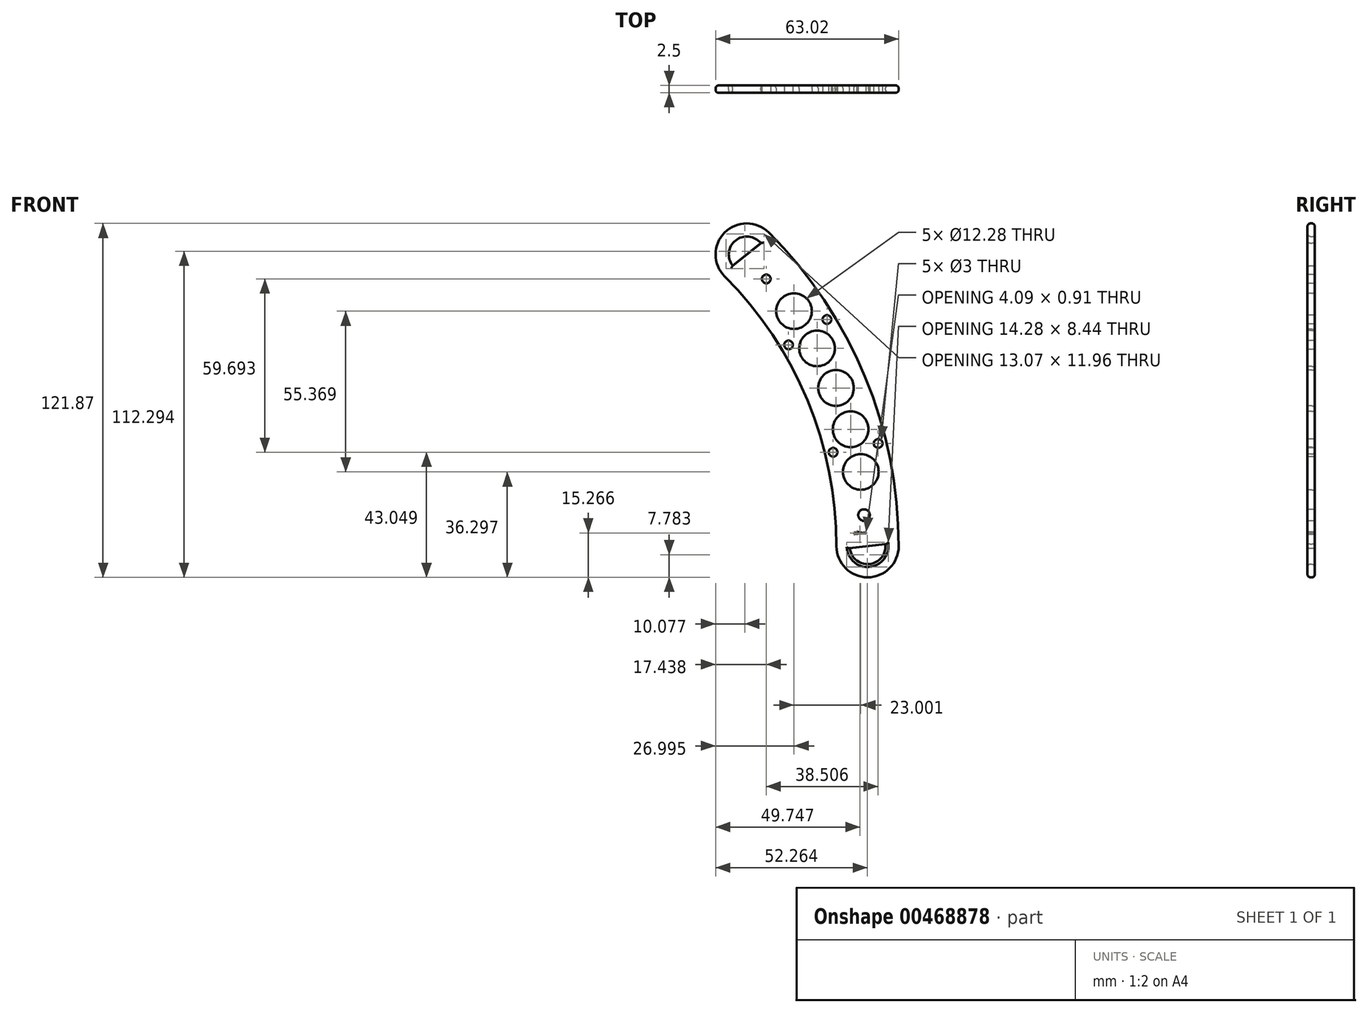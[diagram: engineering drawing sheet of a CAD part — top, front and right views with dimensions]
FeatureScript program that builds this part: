
annotation { "Feature Type Name" : "Feature", "Feature Type Description" : "" }
export const myFeature = defineFeature(function(context is Context, id is Id, definition is map)
    precondition{}
    {
        {
            var Q0;
            Q0=qCreatedBy(makeId("Front.planeOp"),FACE);
            var sketch = newSketch(context, id + "F0", { "sketchPlane" : qUnion([Q0])});
            skCircle(sketch, "E0", {"center": v(0, 0) * mm, "radius": 152.8 * mm});
            skCircle(sketch, "E1", {"center": v(0, 0) * mm, "radius": 131.4 * mm});
            skLineSegment(sketch, "E2", {"start": v(0, 0) * mm, "end": v(152.8, 0) * mm, "construction": true});
            skLineSegment(sketch, "E3", {"start": v(0, 0) * mm, "end": v(108.04, 108.04) * mm, "construction": true});
            skPoint(sketch, "E4", {"position": v(92.9, 92.9) * mm});
            skPoint(sketch, "E5", {"position": v(108.04, 108.04) * mm});
            skPoint(sketch, "E6", {"position": v(131.4, 0) * mm});
            skPoint(sketch, "E7", {"position": v(152.8, 0) * mm});
            skCircle(sketch, "E8", {"center": v(100.47, 100.47) * mm, "radius": 10.7 * mm});
            skCircle(sketch, "E9", {"center": v(142.1, 0) * mm, "radius": 10.7 * mm});
            skLineSegment(sketch, "E10", {"start": v(142.1, 0) * mm, "end": v(148.23, 0.7) * mm});
            skLineSegment(sketch, "E11", {"start": v(142.1, 0) * mm, "end": v(135.94, -0.7) * mm});
            skLineSegment(sketch, "E12", {"start": v(148.23, 0.7) * mm, "end": v(144.58, 32.71) * mm});
            skLineSegment(sketch, "E13", {"start": v(135.94, -0.7) * mm, "end": v(132.3, 31.31) * mm});
            skLineSegment(sketch, "E14", {"start": v(132.3, 31.31) * mm, "end": v(144.58, 32.71) * mm});
            skLineSegment(sketch, "E15", {"start": v(100.47, 100.47) * mm, "end": v(105.3, 104.33) * mm});
            skLineSegment(sketch, "E16", {"start": v(100.47, 100.47) * mm, "end": v(95.64, 96.62) * mm});
            skLineSegment(sketch, "E17", {"start": v(120.53, 75.25) * mm, "end": v(125.41, 79.16) * mm});
            skLineSegment(sketch, "E18", {"start": v(120.53, 75.25) * mm, "end": v(115.75, 71.44) * mm});
            skLineSegment(sketch, "E19", {"start": v(105.3, 104.33) * mm, "end": v(125.41, 79.16) * mm});
            skLineSegment(sketch, "E20", {"start": v(95.64, 96.62) * mm, "end": v(115.75, 71.44) * mm});
            skLineSegment(sketch, "E21", {"start": v(135.42, 3.88) * mm, "end": v(147.7, 5.28) * mm});
            skLineSegment(sketch, "E22", {"start": v(132.82, 26.73) * mm, "end": v(145.1, 28.13) * mm});
            skLineSegment(sketch, "E23", {"start": v(112.88, 75.04) * mm, "end": v(122.53, 82.76) * mm});
            skLineSegment(sketch, "E24", {"start": v(98.52, 93.01) * mm, "end": v(108.18, 100.73) * mm});
            skCircle(sketch, "E25", {"center": v(0, 0) * mm, "radius": 148.23 * mm, "construction": true});
            skCircle(sketch, "E26", {"center": v(0, 0) * mm, "radius": 135.95 * mm, "construction": true});
            skCircle(sketch, "E27", {"center": v(141.82, 2.29) * mm, "radius": 1 * mm});
            skCircle(sketch, "E28", {"center": v(138.7, 29.72) * mm, "radius": 1 * mm});
            skCircle(sketch, "E29", {"center": v(140.86, 10.72) * mm, "radius": 6.18 * mm});
            skLineSegment(sketch, "E30", {"start": v(122.53, 82.76) * mm, "end": v(115.75, 71.44) * mm, "construction": true});
            skLineSegment(sketch, "E31", {"start": v(112.88, 75.04) * mm, "end": v(125.41, 79.16) * mm, "construction": true});
            skCircle(sketch, "E32", {"center": v(101.91, 98.67) * mm, "radius": 1 * mm});
            skCircle(sketch, "E33", {"center": v(119.14, 77.1) * mm, "radius": 1 * mm});
            skCircle(sketch, "E34", {"center": v(107.2, 92.04) * mm, "radius": 6.18 * mm});
            skLineSegment(sketch, "E35", {"start": v(132.82, 26.73) * mm, "end": v(144.58, 32.71) * mm, "construction": true});
            skLineSegment(sketch, "E36", {"start": v(145.1, 28.13) * mm, "end": v(132.3, 31.31) * mm, "construction": true});
            skCircle(sketch, "E37", {"center": v(100.47, 100.47) * mm, "radius": 6.18 * mm});
            skCircle(sketch, "E38", {"center": v(142.1, 0) * mm, "radius": 6.19 * mm});
            skLineSegment(sketch, "E39", {"start": v(135.42, 3.88) * mm, "end": v(148.23, 0.7) * mm, "construction": true});
            skLineSegment(sketch, "E40", {"start": v(147.7, 5.28) * mm, "end": v(135.94, -0.7) * mm, "construction": true});
            skLineSegment(sketch, "E41", {"start": v(148.23, 0.7) * mm, "end": v(148.24, 0.7) * mm});
            skSolve(sketch);
        }
        {
            var Q0;
            {var subQ16=sQuery(id+"F0.wireOp",EDGE,"E18");Q0=makeQuery(id+"F0.imprint","IMPRINT",FACE,{"disambiguationData":[TD([[makeQuery(id+"F0.imprint","IMPRINT",EDGE,{"derivedFrom":subQ16}),1.0]])]});}
            var Q1;
            {var subQ14=sQuery(id+"F0.wireOp",EDGE,"E17");Q1=makeQuery(id+"F0.imprint","IMPRINT",FACE,{"disambiguationData":[TD([[makeQuery(id+"F0.imprint","IMPRINT",EDGE,{"derivedFrom":subQ14}),-1.0]])]});}
            var Q2;
            {var subQ3=sQuery(id+"F0.wireOp",EDGE,"oQQra7B9-EMDj-B2YQ-GpEd-beqhVWcHA2Qh");var subQ5=sQuery(id+"F0.wireOp",EDGE,"E22");var subQ9=makeQuery(id+"F0.imprint","INTERSECT",VERTEX,{"derivedFrom":[subQ3,subQ5]});Q2=makeQuery(id+"F0.imprint","IMPRINT",FACE,{"disambiguationData":[TD([[makeQuery(id+"F0.imprint","IMPRINT",EDGE,{"disambiguationData":[TD([[subQ9,-1.0]])],"derivedFrom":subQ3}),-1.0]])]});}
            var Q3;
            {var subQ3=sQuery(id+"F0.wireOp",EDGE,"oQQra7B9-EMDj-B2YQ-GpEd-beqhVWcHA2Qh");var subQ5=sQuery(id+"F0.wireOp",EDGE,"E22");var subQ9=makeQuery(id+"F0.imprint","INTERSECT",VERTEX,{"derivedFrom":[subQ3,subQ5]});Q3=makeQuery(id+"F0.imprint","IMPRINT",FACE,{"disambiguationData":[TD([[makeQuery(id+"F0.imprint","IMPRINT",EDGE,{"disambiguationData":[TD([[subQ9,-1.0]])],"derivedFrom":subQ3}),1.0]])]});}
            var Q4;
            {var subQ5=sQuery(id+"F0.wireOp",EDGE,"E9");var subQ8=makeQuery(id+"F0.imprint","INTERSECT",VERTEX,{"derivedFrom":[sQuery(id+"F0.wireOp",EDGE,"E1"),subQ5]});Q4=makeQuery(id+"F0.imprint","IMPRINT",FACE,{"disambiguationData":[TD([[makeQuery(id+"F0.imprint","IMPRINT",EDGE,{"disambiguationData":[TD([[subQ8,1.0]])],"derivedFrom":subQ5}),1.0]])]});}
            var Q5;
            {var subQ1=sQuery(id+"F0.wireOp",EDGE,"E9");var subQ5=makeQuery(id+"F0.imprint","INTERSECT",VERTEX,{"derivedFrom":[sQuery(id+"F0.wireOp",EDGE,"E0"),subQ1]});Q5=makeQuery(id+"F0.imprint","IMPRINT",FACE,{"disambiguationData":[TD([[makeQuery(id+"F0.imprint","IMPRINT",EDGE,{"disambiguationData":[TD([[subQ5,-1.0]])],"derivedFrom":subQ1}),1.0]])]});}
            var Q6;
            {var subQ1=sQuery(id+"F0.wireOp",EDGE,"E13");var subQ3=sQuery(id+"F0.wireOp",EDGE,"E21");var subQ4=makeQuery(id+"F0.imprint","INTERSECT",VERTEX,{"derivedFrom":[subQ1,subQ3]});Q6=makeQuery(id+"F0.imprint","IMPRINT",FACE,{"disambiguationData":[TD([[makeQuery(id+"F0.imprint","IMPRINT",EDGE,{"disambiguationData":[TD([[subQ4,-1.0]])],"derivedFrom":subQ3}),-1.0]])]});}
            var Q7;
            {var subQ1=sQuery(id+"F0.wireOp",EDGE,"E12");var subQ3=sQuery(id+"F0.wireOp",EDGE,"E21");var subQ4=makeQuery(id+"F0.imprint","INTERSECT",VERTEX,{"derivedFrom":[subQ1,subQ3]});Q7=makeQuery(id+"F0.imprint","IMPRINT",FACE,{"disambiguationData":[TD([[makeQuery(id+"F0.imprint","IMPRINT",EDGE,{"disambiguationData":[TD([[subQ4,1.0]])],"derivedFrom":subQ3}),-1.0]])]});}
            var Q8;
            {var subQ4=sQuery(id+"F0.wireOp",EDGE,"E8");var subQ5=makeQuery(id+"F0.imprint","INTERSECT",VERTEX,{"derivedFrom":[sQuery(id+"F0.wireOp",EDGE,"E0"),subQ4]});Q8=makeQuery(id+"F0.imprint","IMPRINT",FACE,{"disambiguationData":[TD([[makeQuery(id+"F0.imprint","IMPRINT",EDGE,{"disambiguationData":[TD([[subQ5,-1.0]])],"derivedFrom":subQ4}),1.0]])]});}
            var Q9;
            {var subQ5=sQuery(id+"F0.wireOp",EDGE,"E8");var subQ9=makeQuery(id+"F0.imprint","INTERSECT",VERTEX,{"derivedFrom":[sQuery(id+"F0.wireOp",EDGE,"E1"),subQ5]});Q9=makeQuery(id+"F0.imprint","IMPRINT",FACE,{"disambiguationData":[TD([[makeQuery(id+"F0.imprint","IMPRINT",EDGE,{"disambiguationData":[TD([[subQ9,1.0]])],"derivedFrom":subQ5}),1.0]])]});}
            var Q10;
            {var subQ1=sQuery(id+"F0.wireOp",EDGE,"E20");var subQ3=sQuery(id+"F0.wireOp",EDGE,"E24");var subQ4=makeQuery(id+"F0.imprint","INTERSECT",VERTEX,{"derivedFrom":[subQ1,subQ3]});Q10=makeQuery(id+"F0.imprint","IMPRINT",FACE,{"disambiguationData":[TD([[makeQuery(id+"F0.imprint","IMPRINT",EDGE,{"disambiguationData":[TD([[subQ4,-1.0]])],"derivedFrom":subQ3}),1.0]])]});}
            var Q11;
            {var subQ4=sQuery(id+"F0.wireOp",EDGE,"E16");Q11=makeQuery(id+"F0.imprint","IMPRINT",FACE,{"disambiguationData":[TD([[makeQuery(id+"F0.imprint","IMPRINT",EDGE,{"derivedFrom":subQ4}),1.0]])]});}
            var Q12;
            {var subQ0=sQuery(id+"F0.wireOp",EDGE,"E15");Q12=makeQuery(id+"F0.imprint","IMPRINT",FACE,{"disambiguationData":[TD([[makeQuery(id+"F0.imprint","IMPRINT",EDGE,{"derivedFrom":subQ0}),-1.0]])]});}
            var Q13;
            {var subQ1=sQuery(id+"F0.wireOp",EDGE,"E19");var subQ3=sQuery(id+"F0.wireOp",EDGE,"E24");var subQ4=makeQuery(id+"F0.imprint","INTERSECT",VERTEX,{"derivedFrom":[subQ1,subQ3]});Q13=makeQuery(id+"F0.imprint","IMPRINT",FACE,{"disambiguationData":[TD([[makeQuery(id+"F0.imprint","IMPRINT",EDGE,{"disambiguationData":[TD([[subQ4,1.0]])],"derivedFrom":subQ3}),1.0]])]});}
            var Q14;
            {var subQ1=sQuery(id+"F0.wireOp",EDGE,"E18");Q14=makeQuery(id+"F0.imprint","IMPRINT",FACE,{"disambiguationData":[TD([[makeQuery(id+"F0.imprint","IMPRINT",EDGE,{"derivedFrom":subQ1}),-1.0]])]});}
            var Q15;
            {var subQ1=sQuery(id+"F0.wireOp",EDGE,"E17");Q15=makeQuery(id+"F0.imprint","IMPRINT",FACE,{"disambiguationData":[TD([[makeQuery(id+"F0.imprint","IMPRINT",EDGE,{"derivedFrom":subQ1}),1.0]])]});}
            var Q16;
            {var subQ0=sQuery(id+"F0.wireOp",EDGE,"E14");Q16=makeQuery(id+"F0.imprint","IMPRINT",FACE,{"disambiguationData":[TD([[makeQuery(id+"F0.imprint","IMPRINT",EDGE,{"derivedFrom":subQ0}),-1.0]])]});}
            var Q17;
            {var subQ5=sQuery(id+"F0.wireOp",EDGE,"E10");Q17=makeQuery(id+"F0.imprint","IMPRINT",FACE,{"disambiguationData":[TD([[makeQuery(id+"F0.imprint","IMPRINT",EDGE,{"derivedFrom":subQ5}),1.0]])]});}
            var Q18;
            Q18=makeQuery(id+"F0.imprint","IMPRINT",FACE,{"disambiguationData":[TD([[makeQuery(id+"F0.imprint","IMPRINT",EDGE,{"derivedFrom":sQuery(id+"F0.wireOp",EDGE,"E27")}),-1.0]])]});
            var Q19;
            {var subQ0=sQuery(id+"F0.wireOp",EDGE,"E41");Q19=makeQuery(id+"F0.imprint","IMPRINT",FACE,{"disambiguationData":[TD([[makeQuery(id+"F0.imprint","IMPRINT",EDGE,{"derivedFrom":subQ0}),1.0]])]});}
            extrude(context, id + "F1", {"entities" : qUnion([Q0, Q1, Q2, Q3, Q4, Q5, Q6, Q7, Q8, Q9, Q10, Q11, Q12, Q13, Q14, Q15, Q16, Q17, Q18, Q19]), "depth" : 2.5 * mm});
        }
        {
            var Q0;
            Q0=makeQuery(id+"F1.opExtrude","CAP_FACE",FACE,{"disambiguationData":[OSD([sQuery(id+"F0.wireOp",EDGE,"E0"),sQuery(id+"F0.wireOp",EDGE,"E1"),sQuery(id+"F0.wireOp",EDGE,"E8"),sQuery(id+"F0.wireOp",EDGE,"E9"),sQuery(id+"F0.wireOp",EDGE,"E10"),sQuery(id+"F0.wireOp",EDGE,"E11"),sQuery(id+"F0.wireOp",EDGE,"E12"),sQuery(id+"F0.wireOp",EDGE,"E13"),sQuery(id+"F0.wireOp",EDGE,"E15"),sQuery(id+"F0.wireOp",EDGE,"E16"),sQuery(id+"F0.wireOp",EDGE,"E19"),sQuery(id+"F0.wireOp",EDGE,"E20"),sQuery(id+"F0.wireOp",EDGE,"E21"),sQuery(id+"F0.wireOp",EDGE,"E22"),sQuery(id+"F0.wireOp",EDGE,"E23"),sQuery(id+"F0.wireOp",EDGE,"E24"),sQuery(id+"F0.wireOp",EDGE,"E27"),sQuery(id+"F0.wireOp",EDGE,"E28"),sQuery(id+"F0.wireOp",EDGE,"E32"),sQuery(id+"F0.wireOp",EDGE,"E33"),sQuery(id+"F0.wireOp",EDGE,"E37"),sQuery(id+"F0.wireOp",EDGE,"E38")])],"isStart":false});
            var sketch = newSketch(context, id + "F2", { "sketchPlane" : qUnion([Q0])});
            skCircle(sketch, "E42", {"center": v(136.26, 40.28) * mm, "radius": 6.14 * mm});
            skCircle(sketch, "E43", {"center": v(124.7, 68.12) * mm, "radius": 6.14 * mm});
            skCircle(sketch, "E44", {"center": v(131.22, 54.5) * mm, "radius": 6.14 * mm});
            skCircle(sketch, "E45", {"center": v(0, 0) * mm, "radius": 142.1 * mm, "construction": true});
            skLineSegment(sketch, "E46", {"start": v(0, 0) * mm, "end": v(136.26, 40.28) * mm, "construction": true});
            skLineSegment(sketch, "E47", {"start": v(0, 0) * mm, "end": v(131.22, 54.5) * mm, "construction": true});
            skLineSegment(sketch, "E48", {"start": v(0, 0) * mm, "end": v(124.7, 68.12) * mm, "construction": true});
            skCircle(sketch, "E49", {"center": v(0, 0) * mm, "radius": 152.8 * mm, "construction": true});
            skCircle(sketch, "E50", {"center": v(0, 0) * mm, "radius": 131.4 * mm, "construction": true});
            skCircle(sketch, "E51", {"center": v(0, 0) * mm, "radius": 135.95 * mm, "construction": true});
            skCircle(sketch, "E52", {"center": v(0, 0) * mm, "radius": 148.23 * mm, "construction": true});
            skLineSegment(sketch, "E53", {"start": v(112.88, 75.04) * mm, "end": v(119.3, 65.18) * mm, "construction": true});
            skLineSegment(sketch, "E54", {"start": v(119.3, 65.18) * mm, "end": v(118, 79.14) * mm, "construction": true});
            skLineSegment(sketch, "E55", {"start": v(118, 79.14) * mm, "end": v(130.08, 71.07) * mm, "construction": true});
            skLineSegment(sketch, "E56", {"start": v(130.08, 71.07) * mm, "end": v(122.53, 82.76) * mm, "construction": true});
            skLineSegment(sketch, "E57", {"start": v(122.53, 82.76) * mm, "end": v(118, 79.14) * mm});
            skLineSegment(sketch, "E58", {"start": v(112.88, 75.04) * mm, "end": v(118, 79.14) * mm});
            skLineSegment(sketch, "E59", {"start": v(126.3, 76.91) * mm, "end": v(130.43, 79.57) * mm, "construction": true});
            skCircle(sketch, "E60", {"center": v(128.1, 78.07) * mm, "radius": 1 * mm});
            skLineSegment(sketch, "E61", {"start": v(130.37, 38.54) * mm, "end": v(132.82, 26.73) * mm});
            skLineSegment(sketch, "E62", {"start": v(145.1, 28.13) * mm, "end": v(142.22, 41.78) * mm});
            skLineSegment(sketch, "E63", {"start": v(131.6, 32.64) * mm, "end": v(127.49, 31.79) * mm});
            skLineSegment(sketch, "E64", {"start": v(143.66, 34.96) * mm, "end": v(148.5, 35.98) * mm});
            skCircle(sketch, "E65", {"center": v(130.21, 32.35) * mm, "radius": 1 * mm});
            skCircle(sketch, "E66", {"center": v(145.71, 35.4) * mm, "radius": 1 * mm});
            skLineSegment(sketch, "E67", {"start": v(116.1, 70.11) * mm, "end": v(112.55, 67.8) * mm, "construction": true});
            skCircle(sketch, "E68", {"center": v(114.87, 69.32) * mm, "radius": 1 * mm});
            skLineSegment(sketch, "E69", {"start": v(0, 0) * mm, "end": v(116.76, 80.97) * mm, "construction": true});
            skLineSegment(sketch, "E70", {"start": v(0, 0) * mm, "end": v(139.77, 25.6) * mm, "construction": true});
            skCircle(sketch, "E71", {"center": v(139.77, 25.6) * mm, "radius": 6.14 * mm});
            skCircle(sketch, "E72", {"center": v(116.76, 80.97) * mm, "radius": 6.14 * mm});
            skSolve(sketch);
        }
        {
            var Q0;
            Q0=makeQuery(id+"F2.imprint","IMPRINT",FACE,{"disambiguationData":[TD([[makeQuery(id+"F2.imprint","IMPRINT",EDGE,{"derivedFrom":sQuery(id+"F2.wireOp",EDGE,"E43")}),1.0]])]});
            var Q1;
            Q1=makeQuery(id+"F2.imprint","IMPRINT",FACE,{"disambiguationData":[TD([[makeQuery(id+"F2.imprint","IMPRINT",EDGE,{"derivedFrom":sQuery(id+"F2.wireOp",EDGE,"E44")}),1.0]])]});
            var Q2;
            Q2=makeQuery(id+"F2.imprint","IMPRINT",FACE,{"disambiguationData":[TD([[makeQuery(id+"F2.imprint","IMPRINT",EDGE,{"derivedFrom":sQuery(id+"F2.wireOp",EDGE,"E42")}),1.0]])]});
            var Q3;
            {var subQ0=sQuery(id+"F2.wireOp",EDGE,"E56");var subQ1=sQuery(id+"F2.wireOp",EDGE,"E43");var subQ2=makeQuery(id+"F2.imprint","INTERSECT",VERTEX,{"derivedFrom":[subQ1,subQ0]});Q3=makeQuery(id+"F2.imprint","IMPRINT",FACE,{"disambiguationData":[TD([[makeQuery(id+"F2.imprint","IMPRINT",EDGE,{"disambiguationData":[TD([[subQ2,-1.0]])],"derivedFrom":subQ1}),1.0]])]});}
            var Q4;
            {var subQ0=sQuery(id+"F2.wireOp",EDGE,"E54");var subQ1=sQuery(id+"F2.wireOp",EDGE,"E43");var subQ3=makeQuery(id+"F2.imprint","INTERSECT",VERTEX,{"derivedFrom":[subQ1,subQ0]});Q4=makeQuery(id+"F2.imprint","IMPRINT",FACE,{"disambiguationData":[TD([[makeQuery(id+"F2.imprint","IMPRINT",EDGE,{"disambiguationData":[TD([[subQ3,-1.0]])],"derivedFrom":subQ1}),1.0]])]});}
            var Q5;
            Q5=makeQuery(id+"F2.imprint","IMPRINT",FACE,{"disambiguationData":[TD([[makeQuery(id+"F2.imprint","IMPRINT",EDGE,{"derivedFrom":sQuery(id+"F2.wireOp",EDGE,"6Q9i7ZKX-M5Zn-dDvE-S5ua-DKoOSJd4rO0q")}),1.0]])]});
            var Q6;
            Q6=makeQuery(id+"F2.imprint","IMPRINT",FACE,{"disambiguationData":[TD([[makeQuery(id+"F2.imprint","IMPRINT",EDGE,{"derivedFrom":sQuery(id+"F2.wireOp",EDGE,"E60")}),1.0]])]});
            var Q7;
            Q7=makeQuery(id+"F2.imprint","IMPRINT",FACE,{"disambiguationData":[TD([[makeQuery(id+"F2.imprint","IMPRINT",EDGE,{"derivedFrom":sQuery(id+"F2.wireOp",EDGE,"E68")}),1.0]])]});
            var Q8;
            {var subQ0=sQuery(id+"F2.wireOp",EDGE,"E66");var subQ1=sQuery(id+"F2.wireOp",EDGE,"E64");var subQ2=makeQuery(id+"F2.imprint","INTERSECT",VERTEX,{"disambiguationData":[OD(0.0)],"derivedFrom":[subQ1,subQ0]});Q8=makeQuery(id+"F2.imprint","IMPRINT",FACE,{"disambiguationData":[TD([[makeQuery(id+"F2.imprint","IMPRINT",EDGE,{"disambiguationData":[TD([[subQ2,-1.0]])],"derivedFrom":subQ1}),1.0]])]});}
            var Q9;
            {var subQ0=sQuery(id+"F2.wireOp",EDGE,"E66");var subQ1=sQuery(id+"F2.wireOp",EDGE,"E64");var subQ2=makeQuery(id+"F2.imprint","INTERSECT",VERTEX,{"disambiguationData":[OD(0.0)],"derivedFrom":[subQ1,subQ0]});Q9=makeQuery(id+"F2.imprint","IMPRINT",FACE,{"disambiguationData":[TD([[makeQuery(id+"F2.imprint","IMPRINT",EDGE,{"disambiguationData":[TD([[subQ2,-1.0]])],"derivedFrom":subQ1}),-1.0]])]});}
            var Q10;
            {var subQ0=sQuery(id+"F2.wireOp",EDGE,"E65");var subQ1=sQuery(id+"F2.wireOp",EDGE,"E63");var subQ2=makeQuery(id+"F2.imprint","INTERSECT",VERTEX,{"disambiguationData":[OD(0.0)],"derivedFrom":[subQ1,subQ0]});Q10=makeQuery(id+"F2.imprint","IMPRINT",FACE,{"disambiguationData":[TD([[makeQuery(id+"F2.imprint","IMPRINT",EDGE,{"disambiguationData":[TD([[subQ2,-1.0]])],"derivedFrom":subQ1}),1.0]])]});}
            var Q11;
            {var subQ0=sQuery(id+"F2.wireOp",EDGE,"E65");var subQ1=sQuery(id+"F2.wireOp",EDGE,"E63");var subQ2=makeQuery(id+"F2.imprint","INTERSECT",VERTEX,{"disambiguationData":[OD(0.0)],"derivedFrom":[subQ1,subQ0]});Q11=makeQuery(id+"F2.imprint","IMPRINT",FACE,{"disambiguationData":[TD([[makeQuery(id+"F2.imprint","IMPRINT",EDGE,{"disambiguationData":[TD([[subQ2,-1.0]])],"derivedFrom":subQ1}),-1.0]])]});}
            extrude(context, id + "F3", {"entities" : qUnion([Q0, Q1, Q2, Q3, Q4, Q5, Q6, Q7, Q8, Q9, Q10, Q11]), "operationType" : NewBodyOperationType.REMOVE, "oppositeDirection" : true, "depth" : 25 * mm});
        }
        {
            var Q0;
            Q0=makeQuery(id+"F1.opExtrude","CAP_EDGE",EDGE,{"disambiguationData":[OSD([sQuery(id+"F0.wireOp",EDGE,"E38")])],"isStart":true});
            var Q1;
            Q1=makeQuery(id+"F1.opExtrude","CAP_EDGE",EDGE,{"disambiguationData":[OSD([sQuery(id+"F0.wireOp",EDGE,"E38")])],"isStart":false});
            var Q2;
            Q2=makeQuery(id+"F1.opExtrude","CAP_EDGE",EDGE,{"disambiguationData":[OSD([sQuery(id+"F0.wireOp",EDGE,"E9")])],"isStart":true});
            var Q3;
            Q3=makeQuery(id+"F1.opExtrude","CAP_EDGE",EDGE,{"disambiguationData":[OSD([sQuery(id+"F0.wireOp",EDGE,"E0")])],"isStart":false});
            var Q4;
            Q4=makeQuery(id+"F1.opExtrude","CAP_EDGE",EDGE,{"disambiguationData":[OSD([sQuery(id+"F0.wireOp",EDGE,"E37")])],"isStart":false});
            var Q5;
            Q5=makeQuery(id+"F1.opExtrude","CAP_EDGE",EDGE,{"disambiguationData":[OSD([sQuery(id+"F0.wireOp",EDGE,"E37")])],"isStart":true});
            var Q6;
            Q6=makeQuery(id+"F3.boolean.opBoolean","COPY",EDGE,{"derivedFrom":makeQuery(id+"F3.opExtrude","CAP_EDGE",EDGE,{"disambiguationData":[OSD([sQuery(id+"F2.wireOp",EDGE,"E43")])],"isStart":true})});
            var Q7;
            Q7=makeQuery(id+"F3.boolean.opBoolean","COPY",EDGE,{"derivedFrom":makeQuery(id+"F3.opExtrude","CAP_EDGE",EDGE,{"disambiguationData":[OSD([sQuery(id+"F2.wireOp",EDGE,"E44")])],"isStart":true})});
            var Q8;
            Q8=makeQuery(id+"F3.boolean.opBoolean","COPY",EDGE,{"derivedFrom":makeQuery(id+"F3.opExtrude","CAP_EDGE",EDGE,{"disambiguationData":[OSD([sQuery(id+"F2.wireOp",EDGE,"E42")])],"isStart":true})});
            var Q9;
            Q9=makeQuery(id+"F3.boolean.opBoolean","INTERSECT",EDGE,{"derivedFrom":[makeQuery(id+"F1.opExtrude","CAP_FACE",FACE,{"disambiguationData":[OSD([sQuery(id+"F0.wireOp",EDGE,"E0"),sQuery(id+"F0.wireOp",EDGE,"E1"),sQuery(id+"F0.wireOp",EDGE,"E8"),sQuery(id+"F0.wireOp",EDGE,"E9"),sQuery(id+"F0.wireOp",EDGE,"E10"),sQuery(id+"F0.wireOp",EDGE,"E11"),sQuery(id+"F0.wireOp",EDGE,"E12"),sQuery(id+"F0.wireOp",EDGE,"E13"),sQuery(id+"F0.wireOp",EDGE,"E15"),sQuery(id+"F0.wireOp",EDGE,"E16"),sQuery(id+"F0.wireOp",EDGE,"E19"),sQuery(id+"F0.wireOp",EDGE,"E20"),sQuery(id+"F0.wireOp",EDGE,"E21"),sQuery(id+"F0.wireOp",EDGE,"E22"),sQuery(id+"F0.wireOp",EDGE,"E23"),sQuery(id+"F0.wireOp",EDGE,"E24"),sQuery(id+"F0.wireOp",EDGE,"E27"),sQuery(id+"F0.wireOp",EDGE,"E28"),sQuery(id+"F0.wireOp",EDGE,"E32"),sQuery(id+"F0.wireOp",EDGE,"E33"),sQuery(id+"F0.wireOp",EDGE,"E37"),sQuery(id+"F0.wireOp",EDGE,"E38")])],"isStart":true}),makeQuery(id+"F3.opExtrude","SWEPT_FACE",FACE,{"disambiguationData":[OSD([sQuery(id+"F2.wireOp",EDGE,"E43")])]})]});
            var Q10;
            Q10=makeQuery(id+"F3.boolean.opBoolean","INTERSECT",EDGE,{"derivedFrom":[makeQuery(id+"F1.opExtrude","CAP_FACE",FACE,{"disambiguationData":[OSD([sQuery(id+"F0.wireOp",EDGE,"E0"),sQuery(id+"F0.wireOp",EDGE,"E1"),sQuery(id+"F0.wireOp",EDGE,"E8"),sQuery(id+"F0.wireOp",EDGE,"E9"),sQuery(id+"F0.wireOp",EDGE,"E10"),sQuery(id+"F0.wireOp",EDGE,"E11"),sQuery(id+"F0.wireOp",EDGE,"E12"),sQuery(id+"F0.wireOp",EDGE,"E13"),sQuery(id+"F0.wireOp",EDGE,"E15"),sQuery(id+"F0.wireOp",EDGE,"E16"),sQuery(id+"F0.wireOp",EDGE,"E19"),sQuery(id+"F0.wireOp",EDGE,"E20"),sQuery(id+"F0.wireOp",EDGE,"E21"),sQuery(id+"F0.wireOp",EDGE,"E22"),sQuery(id+"F0.wireOp",EDGE,"E23"),sQuery(id+"F0.wireOp",EDGE,"E24"),sQuery(id+"F0.wireOp",EDGE,"E27"),sQuery(id+"F0.wireOp",EDGE,"E28"),sQuery(id+"F0.wireOp",EDGE,"E32"),sQuery(id+"F0.wireOp",EDGE,"E33"),sQuery(id+"F0.wireOp",EDGE,"E37"),sQuery(id+"F0.wireOp",EDGE,"E38")])],"isStart":true}),makeQuery(id+"F3.opExtrude","SWEPT_FACE",FACE,{"disambiguationData":[OSD([sQuery(id+"F2.wireOp",EDGE,"E44")])]})]});
            var Q11;
            Q11=makeQuery(id+"F3.boolean.opBoolean","INTERSECT",EDGE,{"derivedFrom":[makeQuery(id+"F1.opExtrude","CAP_FACE",FACE,{"disambiguationData":[OSD([sQuery(id+"F0.wireOp",EDGE,"E0"),sQuery(id+"F0.wireOp",EDGE,"E1"),sQuery(id+"F0.wireOp",EDGE,"E8"),sQuery(id+"F0.wireOp",EDGE,"E9"),sQuery(id+"F0.wireOp",EDGE,"E10"),sQuery(id+"F0.wireOp",EDGE,"E11"),sQuery(id+"F0.wireOp",EDGE,"E12"),sQuery(id+"F0.wireOp",EDGE,"E13"),sQuery(id+"F0.wireOp",EDGE,"E15"),sQuery(id+"F0.wireOp",EDGE,"E16"),sQuery(id+"F0.wireOp",EDGE,"E19"),sQuery(id+"F0.wireOp",EDGE,"E20"),sQuery(id+"F0.wireOp",EDGE,"E21"),sQuery(id+"F0.wireOp",EDGE,"E22"),sQuery(id+"F0.wireOp",EDGE,"E23"),sQuery(id+"F0.wireOp",EDGE,"E24"),sQuery(id+"F0.wireOp",EDGE,"E27"),sQuery(id+"F0.wireOp",EDGE,"E28"),sQuery(id+"F0.wireOp",EDGE,"E32"),sQuery(id+"F0.wireOp",EDGE,"E33"),sQuery(id+"F0.wireOp",EDGE,"E37"),sQuery(id+"F0.wireOp",EDGE,"E38")])],"isStart":true}),makeQuery(id+"F3.opExtrude","SWEPT_FACE",FACE,{"disambiguationData":[OSD([sQuery(id+"F2.wireOp",EDGE,"E42")])]})]});
            fillet(context, id + "F4", {"entities" : qUnion([Q0, Q1, Q2, Q3, Q4, Q5, Q6, Q7, Q8, Q9, Q10, Q11]), "radius" : 1 * mm, "tangentPropagation" : true, "allowEdgeOverflow" : false});
        }
        {
            var Q0;
            Q0=makeQuery(id+"F1.opExtrude","CAP_EDGE",EDGE,{"disambiguationData":[OSD([sQuery(id+"F0.wireOp",EDGE,"E15"),sQuery(id+"F0.wireOp",EDGE,"E16")])],"isStart":false});
            var Q1;
            Q1=makeQuery(id+"F1.opExtrude","CAP_EDGE",EDGE,{"disambiguationData":[OSD([sQuery(id+"F0.wireOp",EDGE,"E15"),sQuery(id+"F0.wireOp",EDGE,"E16")])],"isStart":true});
            var Q2;
            Q2=makeQuery(id+"F1.opExtrude","CAP_EDGE",EDGE,{"disambiguationData":[OSD([sQuery(id+"F0.wireOp",EDGE,"E10"),sQuery(id+"F0.wireOp",EDGE,"E11")])],"isStart":true});
            var Q3;
            Q3=makeQuery(id+"F1.opExtrude","CAP_EDGE",EDGE,{"disambiguationData":[OSD([sQuery(id+"F0.wireOp",EDGE,"E10"),sQuery(id+"F0.wireOp",EDGE,"E11")])],"isStart":false});
            fillet(context, id + "F5", {"entities" : qUnion([Q0, Q1, Q2, Q3]), "radius" : 0.5 * mm, "tangentPropagation" : true, "allowEdgeOverflow" : false});
        }
        {
            var Q0;
            {var subQ1=sQuery(id+"F0.wireOp",EDGE,"E9");var subQ6=sQuery(id+"F0.wireOp",EDGE,"E12");var subQ8=makeQuery(id+"F0.imprint","INTERSECT",VERTEX,{"derivedFrom":[subQ1,subQ6]});Q0=makeQuery(id+"F0.imprint","IMPRINT",FACE,{"disambiguationData":[TD([[makeQuery(id+"F0.imprint","IMPRINT",EDGE,{"disambiguationData":[TD([[subQ8,-1.0]])],"derivedFrom":subQ1}),1.0]])]});}
            var Q1;
            {var subQ0=sQuery(id+"F0.wireOp",EDGE,"E29");var subQ1=sQuery(id+"F0.wireOp",EDGE,"E9");var subQ2=makeQuery(id+"F0.imprint","INTERSECT",VERTEX,{"disambiguationData":[OD(0.0)],"derivedFrom":[subQ1,subQ0]});Q1=makeQuery(id+"F0.imprint","IMPRINT",FACE,{"disambiguationData":[TD([[makeQuery(id+"F0.imprint","IMPRINT",EDGE,{"disambiguationData":[TD([[subQ2,-1.0]])],"derivedFrom":subQ1}),-1.0]])]});}
            var Q2;
            {var subQ0=sQuery(id+"F0.wireOp",EDGE,"E29");var subQ1=sQuery(id+"F0.wireOp",EDGE,"E9");var subQ2=makeQuery(id+"F0.imprint","INTERSECT",VERTEX,{"disambiguationData":[OD(0.0)],"derivedFrom":[subQ1,subQ0]});Q2=makeQuery(id+"F0.imprint","IMPRINT",FACE,{"disambiguationData":[TD([[makeQuery(id+"F0.imprint","IMPRINT",EDGE,{"disambiguationData":[TD([[subQ2,-1.0]])],"derivedFrom":subQ1}),1.0]])]});}
            var Q3;
            {var subQ0=sQuery(id+"F0.wireOp",EDGE,"E29");var subQ1=makeQuery(id+"F0.imprint","INTERSECT",VERTEX,{"derivedFrom":[sQuery(id+"F0.wireOp",EDGE,"E21"),subQ0]});Q3=makeQuery(id+"F0.imprint","IMPRINT",FACE,{"disambiguationData":[TD([[makeQuery(id+"F0.imprint","IMPRINT",EDGE,{"disambiguationData":[TD([[subQ1,1.0]])],"derivedFrom":subQ0}),1.0]])]});}
            var Q4;
            {var subQ0=sQuery(id+"F0.wireOp",EDGE,"E29");var subQ1=sQuery(id+"F0.wireOp",EDGE,"E9");var subQ2=makeQuery(id+"F0.imprint","INTERSECT",VERTEX,{"disambiguationData":[OD(1.0)],"derivedFrom":[subQ1,subQ0]});Q4=makeQuery(id+"F0.imprint","IMPRINT",FACE,{"disambiguationData":[TD([[makeQuery(id+"F0.imprint","IMPRINT",EDGE,{"disambiguationData":[TD([[subQ2,-1.0]])],"derivedFrom":subQ1}),1.0]])]});}
            var Q5;
            {var subQ0=sQuery(id+"F0.wireOp",EDGE,"E38");var subQ1=sQuery(id+"F0.wireOp",EDGE,"E21");var subQ2=makeQuery(id+"F0.imprint","INTERSECT",VERTEX,{"disambiguationData":[OD(0.0)],"derivedFrom":[subQ1,subQ0]});Q5=makeQuery(id+"F0.imprint","IMPRINT",FACE,{"disambiguationData":[TD([[makeQuery(id+"F0.imprint","IMPRINT",EDGE,{"disambiguationData":[TD([[subQ2,-1.0]])],"derivedFrom":subQ1}),1.0]])]});}
            var Q6;
            {var subQ0=sQuery(id+"F0.wireOp",EDGE,"E29");var subQ1=sQuery(id+"F0.wireOp",EDGE,"E21");var subQ2=makeQuery(id+"F0.imprint","INTERSECT",VERTEX,{"derivedFrom":[subQ1,subQ0]});Q6=makeQuery(id+"F0.imprint","IMPRINT",FACE,{"disambiguationData":[TD([[makeQuery(id+"F0.imprint","IMPRINT",EDGE,{"disambiguationData":[TD([[subQ2,-1.0]])],"derivedFrom":subQ1}),1.0]])]});}
            var Q7;
            {var subQ0=sQuery(id+"F0.wireOp",EDGE,"E22");Q7=makeQuery(id+"F0.imprint","IMPRINT",FACE,{"disambiguationData":[TD([[makeQuery(id+"F0.imprint","IMPRINT",EDGE,{"derivedFrom":subQ0}),-1.0]])]});}
            var Q8;
            {var subQ0=sQuery(id+"F0.wireOp",EDGE,"E12");var subQ1=sQuery(id+"F0.wireOp",EDGE,"E9");var subQ2=makeQuery(id+"F0.imprint","INTERSECT",VERTEX,{"derivedFrom":[subQ1,subQ0]});Q8=makeQuery(id+"F0.imprint","IMPRINT",FACE,{"disambiguationData":[TD([[makeQuery(id+"F0.imprint","IMPRINT",EDGE,{"disambiguationData":[TD([[subQ2,-1.0]])],"derivedFrom":subQ1}),-1.0]])]});}
            var Q9;
            {var subQ0=sQuery(id+"F0.wireOp",EDGE,"E29");var subQ1=sQuery(id+"F0.wireOp",EDGE,"E9");var subQ2=makeQuery(id+"F0.imprint","INTERSECT",VERTEX,{"disambiguationData":[OD(1.0)],"derivedFrom":[subQ1,subQ0]});Q9=makeQuery(id+"F0.imprint","IMPRINT",FACE,{"disambiguationData":[TD([[makeQuery(id+"F0.imprint","IMPRINT",EDGE,{"disambiguationData":[TD([[subQ2,-1.0]])],"derivedFrom":subQ1}),-1.0]])]});}
            var Q10;
            {var subQ0=sQuery(id+"F0.wireOp",EDGE,"E23");Q10=makeQuery(id+"F0.imprint","IMPRINT",FACE,{"disambiguationData":[TD([[makeQuery(id+"F0.imprint","IMPRINT",EDGE,{"derivedFrom":subQ0}),1.0]])]});}
            var Q11;
            {var subQ0=sQuery(id+"F0.wireOp",EDGE,"E34");var subQ1=sQuery(id+"F0.wireOp",EDGE,"E8");var subQ2=makeQuery(id+"F0.imprint","INTERSECT",VERTEX,{"disambiguationData":[OD(0.0)],"derivedFrom":[subQ1,subQ0]});Q11=makeQuery(id+"F0.imprint","IMPRINT",FACE,{"disambiguationData":[TD([[makeQuery(id+"F0.imprint","IMPRINT",EDGE,{"disambiguationData":[TD([[subQ2,-1.0]])],"derivedFrom":subQ1}),-1.0]])]});}
            var Q12;
            {var subQ0=sQuery(id+"F0.wireOp",EDGE,"E34");var subQ1=sQuery(id+"F0.wireOp",EDGE,"E8");var subQ2=makeQuery(id+"F0.imprint","INTERSECT",VERTEX,{"disambiguationData":[OD(0.0)],"derivedFrom":[subQ1,subQ0]});Q12=makeQuery(id+"F0.imprint","IMPRINT",FACE,{"disambiguationData":[TD([[makeQuery(id+"F0.imprint","IMPRINT",EDGE,{"disambiguationData":[TD([[subQ2,-1.0]])],"derivedFrom":subQ1}),1.0]])]});}
            var Q13;
            {var subQ0=sQuery(id+"F0.wireOp",EDGE,"E34");var subQ1=sQuery(id+"F0.wireOp",EDGE,"E8");var subQ2=makeQuery(id+"F0.imprint","INTERSECT",VERTEX,{"disambiguationData":[OD(1.0)],"derivedFrom":[subQ1,subQ0]});Q13=makeQuery(id+"F0.imprint","IMPRINT",FACE,{"disambiguationData":[TD([[makeQuery(id+"F0.imprint","IMPRINT",EDGE,{"disambiguationData":[TD([[subQ2,-1.0]])],"derivedFrom":subQ1}),1.0]])]});}
            var Q14;
            {var subQ0=sQuery(id+"F0.wireOp",EDGE,"E34");var subQ1=sQuery(id+"F0.wireOp",EDGE,"E24");var subQ2=makeQuery(id+"F0.imprint","INTERSECT",VERTEX,{"derivedFrom":[subQ1,subQ0]});Q14=makeQuery(id+"F0.imprint","IMPRINT",FACE,{"disambiguationData":[TD([[makeQuery(id+"F0.imprint","IMPRINT",EDGE,{"disambiguationData":[TD([[subQ2,-1.0]])],"derivedFrom":subQ1}),-1.0]])]});}
            var Q15;
            {var subQ0=sQuery(id+"F0.wireOp",EDGE,"E34");var subQ1=makeQuery(id+"F0.imprint","INTERSECT",VERTEX,{"derivedFrom":[sQuery(id+"F0.wireOp",EDGE,"E24"),subQ0]});Q15=makeQuery(id+"F0.imprint","IMPRINT",FACE,{"disambiguationData":[TD([[makeQuery(id+"F0.imprint","IMPRINT",EDGE,{"disambiguationData":[TD([[subQ1,1.0]])],"derivedFrom":subQ0}),1.0]])]});}
            var Q16;
            {var subQ0=sQuery(id+"F0.wireOp",EDGE,"E37");var subQ1=sQuery(id+"F0.wireOp",EDGE,"E24");var subQ2=makeQuery(id+"F0.imprint","INTERSECT",VERTEX,{"disambiguationData":[OD(0.0)],"derivedFrom":[subQ1,subQ0]});Q16=makeQuery(id+"F0.imprint","IMPRINT",FACE,{"disambiguationData":[TD([[makeQuery(id+"F0.imprint","IMPRINT",EDGE,{"disambiguationData":[TD([[subQ2,-1.0]])],"derivedFrom":subQ1}),-1.0]])]});}
            var Q17;
            {var subQ1=sQuery(id+"F0.wireOp",EDGE,"E8");var subQ6=sQuery(id+"F0.wireOp",EDGE,"E20");var subQ9=makeQuery(id+"F0.imprint","INTERSECT",VERTEX,{"derivedFrom":[subQ1,subQ6]});Q17=makeQuery(id+"F0.imprint","IMPRINT",FACE,{"disambiguationData":[TD([[makeQuery(id+"F0.imprint","IMPRINT",EDGE,{"disambiguationData":[TD([[subQ9,-1.0]])],"derivedFrom":subQ1}),1.0]])]});}
            var Q18;
            {var subQ0=sQuery(id+"F0.wireOp",EDGE,"E34");var subQ1=sQuery(id+"F0.wireOp",EDGE,"E8");var subQ2=makeQuery(id+"F0.imprint","INTERSECT",VERTEX,{"disambiguationData":[OD(1.0)],"derivedFrom":[subQ1,subQ0]});Q18=makeQuery(id+"F0.imprint","IMPRINT",FACE,{"disambiguationData":[TD([[makeQuery(id+"F0.imprint","IMPRINT",EDGE,{"disambiguationData":[TD([[subQ2,-1.0]])],"derivedFrom":subQ1}),-1.0]])]});}
            var Q19;
            {var subQ0=sQuery(id+"F0.wireOp",EDGE,"E20");var subQ1=sQuery(id+"F0.wireOp",EDGE,"E8");var subQ2=makeQuery(id+"F0.imprint","INTERSECT",VERTEX,{"derivedFrom":[subQ1,subQ0]});Q19=makeQuery(id+"F0.imprint","IMPRINT",FACE,{"disambiguationData":[TD([[makeQuery(id+"F0.imprint","IMPRINT",EDGE,{"disambiguationData":[TD([[subQ2,-1.0]])],"derivedFrom":subQ1}),-1.0]])]});}
            extrude(context, id + "F6", {"entities" : qUnion([Q0, Q1, Q2, Q3, Q4, Q5, Q6, Q7, Q8, Q9, Q10, Q11, Q12, Q13, Q14, Q15, Q16, Q17, Q18, Q19]), "operationType" : NewBodyOperationType.ADD, "depth" : 2.5 * mm});
        }
        {
            var Q0;
            {var subQ0=sQuery(id+"F0.wireOp",EDGE,"E24");var subQ1=sQuery(id+"F0.wireOp",EDGE,"E23");var subQ2=sQuery(id+"F0.wireOp",EDGE,"E20");var subQ3=sQuery(id+"F0.wireOp",EDGE,"E19");var subQ4=sQuery(id+"F0.wireOp",EDGE,"E22");var subQ5=sQuery(id+"F0.wireOp",EDGE,"E21");var subQ6=sQuery(id+"F0.wireOp",EDGE,"E13");var subQ7=sQuery(id+"F0.wireOp",EDGE,"E12");Q0=makeQuery(id+"F6.boolean.opBoolean","MERGE",FACE,{"derivedFrom":[makeQuery(id+"F1.opExtrude","CAP_FACE",FACE,{"disambiguationData":[OSD([sQuery(id+"F0.wireOp",EDGE,"E0"),sQuery(id+"F0.wireOp",EDGE,"E1"),sQuery(id+"F0.wireOp",EDGE,"E8"),sQuery(id+"F0.wireOp",EDGE,"E9"),sQuery(id+"F0.wireOp",EDGE,"E10"),sQuery(id+"F0.wireOp",EDGE,"E11"),subQ7,subQ6,sQuery(id+"F0.wireOp",EDGE,"E15"),sQuery(id+"F0.wireOp",EDGE,"E16"),subQ3,subQ2,subQ5,subQ4,subQ1,subQ0,sQuery(id+"F0.wireOp",EDGE,"E27"),sQuery(id+"F0.wireOp",EDGE,"E28"),sQuery(id+"F0.wireOp",EDGE,"E32"),sQuery(id+"F0.wireOp",EDGE,"E33"),sQuery(id+"F0.wireOp",EDGE,"E37"),sQuery(id+"F0.wireOp",EDGE,"E38")])],"isStart":false}),makeQuery(id+"F6.opExtrude","CAP_FACE",FACE,{"disambiguationData":[OSD([subQ7,subQ6,subQ5,subQ4])],"isStart":false}),makeQuery(id+"F6.opExtrude","CAP_FACE",FACE,{"disambiguationData":[OSD([subQ3,subQ2,subQ1,subQ0])],"isStart":false})]});}
            var sketch = newSketch(context, id + "F7", { "sketchPlane" : qUnion([Q0])});
            skCircle(sketch, "E73", {"center": v(140.86, 10.72) * mm, "radius": 2 * mm});
            skCircle(sketch, "E74", {"center": v(107.2, 92.04) * mm, "radius": 2 * mm});
            skSolve(sketch);
        }
        {
            var Q0;
            Q0=qSketchRegion(id+"F7",true);
            extrude(context, id + "F8", {"entities" : qUnion([Q0]), "operationType" : NewBodyOperationType.REMOVE, "oppositeDirection" : true, "depth" : 25 * mm});
        }
        {
            var Q0;
            Q0=makeQuery(id+"F0.imprint","IMPRINT",FACE,{"disambiguationData":[TD([[makeQuery(id+"F0.imprint","IMPRINT",EDGE,{"derivedFrom":sQuery(id+"F0.wireOp",EDGE,"E32")}),1.0]])]});
            var Q1;
            Q1=makeQuery(id+"F0.imprint","IMPRINT",FACE,{"disambiguationData":[TD([[makeQuery(id+"F0.imprint","IMPRINT",EDGE,{"derivedFrom":sQuery(id+"F0.wireOp",EDGE,"E33")}),1.0]])]});
            var Q2;
            Q2=makeQuery(id+"F0.imprint","IMPRINT",FACE,{"disambiguationData":[TD([[makeQuery(id+"F0.imprint","IMPRINT",EDGE,{"derivedFrom":sQuery(id+"F0.wireOp",EDGE,"E28")}),1.0]])]});
            var Q3;
            Q3=makeQuery(id+"F0.imprint","IMPRINT",FACE,{"disambiguationData":[TD([[makeQuery(id+"F0.imprint","IMPRINT",EDGE,{"derivedFrom":sQuery(id+"F0.wireOp",EDGE,"E27")}),1.0]])]});
            extrude(context, id + "F9", {"entities" : qUnion([Q0, Q1, Q2, Q3]), "operationType" : NewBodyOperationType.ADD, "depth" : 2.5 * mm});
        }
        {
            var Q0;
            {var subQ0=sQuery(id+"F2.wireOp",EDGE,"E71");var subQ1=makeQuery(id+"F1.opExtrude","CAP_EDGE",EDGE,{"disambiguationData":[OSD([sQuery(id+"F0.wireOp",EDGE,"E22")])],"isStart":false});var subQ2=makeQuery(id+"F2.imprint","INTERSECT",VERTEX,{"derivedFrom":[subQ1,subQ0]});Q0=makeQuery(id+"F2.imprint","IMPRINT",FACE,{"disambiguationData":[TD([[makeQuery(id+"F2.imprint","IMPRINT",EDGE,{"disambiguationData":[TD([[subQ2,-1.0]])],"derivedFrom":subQ0}),1.0]])]});}
            var Q1;
            Q1=makeQuery(id+"F2.imprint","IMPRINT",FACE,{"disambiguationData":[TD([[makeQuery(id+"F2.imprint","IMPRINT",EDGE,{"derivedFrom":makeQuery(id+"F1.opExtrude","CAP_EDGE",EDGE,{"disambiguationData":[OSD([sQuery(id+"F0.wireOp",EDGE,"E28")])],"isStart":false})}),-1.0]])]});
            var Q2;
            Q2=makeQuery(id+"F2.imprint","IMPRINT",FACE,{"disambiguationData":[TD([[makeQuery(id+"F2.imprint","IMPRINT",EDGE,{"derivedFrom":makeQuery(id+"F1.opExtrude","CAP_EDGE",EDGE,{"disambiguationData":[OSD([sQuery(id+"F0.wireOp",EDGE,"E28")])],"isStart":false})}),1.0]])]});
            var Q3;
            {var subQ0=sQuery(id+"F2.wireOp",EDGE,"E62");var subQ3=sQuery(id+"F2.wireOp",EDGE,"E71");var subQ4=makeQuery(id+"F2.imprint","INTERSECT",VERTEX,{"derivedFrom":[subQ0,subQ3]});Q3=makeQuery(id+"F2.imprint","IMPRINT",FACE,{"disambiguationData":[TD([[makeQuery(id+"F2.imprint","IMPRINT",EDGE,{"disambiguationData":[TD([[subQ4,1.0]])],"derivedFrom":subQ3}),1.0]])]});}
            var Q4;
            {var subQ0=sQuery(id+"F2.wireOp",EDGE,"E57");Q4=makeQuery(id+"F2.imprint","IMPRINT",FACE,{"disambiguationData":[TD([[makeQuery(id+"F2.imprint","IMPRINT",EDGE,{"derivedFrom":subQ0}),1.0]])]});}
            var Q5;
            {var subQ5=sQuery(id+"F2.wireOp",EDGE,"E57");Q5=makeQuery(id+"F2.imprint","IMPRINT",FACE,{"disambiguationData":[TD([[makeQuery(id+"F2.imprint","IMPRINT",EDGE,{"derivedFrom":subQ5}),-1.0]])]});}
            var Q6;
            Q6=makeQuery(id+"F2.imprint","IMPRINT",FACE,{"disambiguationData":[TD([[makeQuery(id+"F2.imprint","IMPRINT",EDGE,{"derivedFrom":makeQuery(id+"F1.opExtrude","CAP_EDGE",EDGE,{"disambiguationData":[OSD([sQuery(id+"F0.wireOp",EDGE,"E33")])],"isStart":false})}),1.0]])]});
            extrude(context, id + "F10", {"entities" : qUnion([Q0, Q1, Q2, Q3, Q4, Q5, Q6]), "operationType" : NewBodyOperationType.REMOVE, "oppositeDirection" : true, "depth" : 25 * mm});
        }
        {
            var Q0;
            Q0=makeQuery(id+"F10.boolean.opBoolean","COPY",EDGE,{"derivedFrom":makeQuery(id+"F10.opExtrude","CAP_EDGE",EDGE,{"disambiguationData":[OSD([sQuery(id+"F2.wireOp",EDGE,"E72")])],"isStart":true})});
            var Q1;
            Q1=makeQuery(id+"F10.boolean.opBoolean","COPY",EDGE,{"derivedFrom":makeQuery(id+"F10.opExtrude","CAP_EDGE",EDGE,{"disambiguationData":[OSD([sQuery(id+"F2.wireOp",EDGE,"E71")])],"isStart":true})});
            var Q2;
            {var subQ0=sQuery(id+"F0.wireOp",EDGE,"E33");var subQ1=sQuery(id+"F0.wireOp",EDGE,"E32");var subQ2=sQuery(id+"F0.wireOp",EDGE,"E28");var subQ3=sQuery(id+"F0.wireOp",EDGE,"E27");var subQ4=sQuery(id+"F0.wireOp",EDGE,"E24");var subQ5=sQuery(id+"F0.wireOp",EDGE,"E23");var subQ6=sQuery(id+"F0.wireOp",EDGE,"E20");var subQ7=sQuery(id+"F0.wireOp",EDGE,"E19");var subQ8=sQuery(id+"F0.wireOp",EDGE,"E22");var subQ9=sQuery(id+"F0.wireOp",EDGE,"E21");var subQ10=sQuery(id+"F0.wireOp",EDGE,"E13");var subQ11=sQuery(id+"F0.wireOp",EDGE,"E12");Q2=makeQuery(id+"F10.boolean.opBoolean","INTERSECT",EDGE,{"derivedFrom":[makeQuery(id+"F9.boolean.opBoolean","MERGE",FACE,{"derivedFrom":[makeQuery(id+"F6.boolean.opBoolean","MERGE",FACE,{"derivedFrom":[makeQuery(id+"F1.opExtrude","CAP_FACE",FACE,{"disambiguationData":[OSD([sQuery(id+"F0.wireOp",EDGE,"E0"),sQuery(id+"F0.wireOp",EDGE,"E1"),sQuery(id+"F0.wireOp",EDGE,"E8"),sQuery(id+"F0.wireOp",EDGE,"E9"),sQuery(id+"F0.wireOp",EDGE,"E10"),sQuery(id+"F0.wireOp",EDGE,"E11"),subQ11,subQ10,sQuery(id+"F0.wireOp",EDGE,"E15"),sQuery(id+"F0.wireOp",EDGE,"E16"),subQ7,subQ6,subQ9,subQ8,subQ5,subQ4,subQ3,subQ2,subQ1,subQ0,sQuery(id+"F0.wireOp",EDGE,"E37"),sQuery(id+"F0.wireOp",EDGE,"E38")])],"isStart":true}),makeQuery(id+"F6.opExtrude","CAP_FACE",FACE,{"disambiguationData":[OSD([subQ11,subQ10,subQ9,subQ8])],"isStart":true}),makeQuery(id+"F6.opExtrude","CAP_FACE",FACE,{"disambiguationData":[OSD([subQ7,subQ6,subQ5,subQ4])],"isStart":true})]}),makeQuery(id+"F9.opExtrude","CAP_FACE",FACE,{"disambiguationData":[OSD([subQ3])],"isStart":true}),makeQuery(id+"F9.opExtrude","CAP_FACE",FACE,{"disambiguationData":[OSD([subQ2])],"isStart":true}),makeQuery(id+"F9.opExtrude","CAP_FACE",FACE,{"disambiguationData":[OSD([subQ1])],"isStart":true}),makeQuery(id+"F9.opExtrude","CAP_FACE",FACE,{"disambiguationData":[OSD([subQ0])],"isStart":true})]}),makeQuery(id+"F10.opExtrude","SWEPT_FACE",FACE,{"disambiguationData":[OSD([sQuery(id+"F2.wireOp",EDGE,"E71")])]})]});}
            var Q3;
            {var subQ0=sQuery(id+"F0.wireOp",EDGE,"E33");var subQ1=sQuery(id+"F0.wireOp",EDGE,"E32");var subQ2=sQuery(id+"F0.wireOp",EDGE,"E28");var subQ3=sQuery(id+"F0.wireOp",EDGE,"E27");var subQ4=sQuery(id+"F0.wireOp",EDGE,"E24");var subQ5=sQuery(id+"F0.wireOp",EDGE,"E23");var subQ6=sQuery(id+"F0.wireOp",EDGE,"E20");var subQ7=sQuery(id+"F0.wireOp",EDGE,"E19");var subQ8=sQuery(id+"F0.wireOp",EDGE,"E22");var subQ9=sQuery(id+"F0.wireOp",EDGE,"E21");var subQ10=sQuery(id+"F0.wireOp",EDGE,"E13");var subQ11=sQuery(id+"F0.wireOp",EDGE,"E12");Q3=makeQuery(id+"F10.boolean.opBoolean","INTERSECT",EDGE,{"derivedFrom":[makeQuery(id+"F9.boolean.opBoolean","MERGE",FACE,{"derivedFrom":[makeQuery(id+"F6.boolean.opBoolean","MERGE",FACE,{"derivedFrom":[makeQuery(id+"F1.opExtrude","CAP_FACE",FACE,{"disambiguationData":[OSD([sQuery(id+"F0.wireOp",EDGE,"E0"),sQuery(id+"F0.wireOp",EDGE,"E1"),sQuery(id+"F0.wireOp",EDGE,"E8"),sQuery(id+"F0.wireOp",EDGE,"E9"),sQuery(id+"F0.wireOp",EDGE,"E10"),sQuery(id+"F0.wireOp",EDGE,"E11"),subQ11,subQ10,sQuery(id+"F0.wireOp",EDGE,"E15"),sQuery(id+"F0.wireOp",EDGE,"E16"),subQ7,subQ6,subQ9,subQ8,subQ5,subQ4,subQ3,subQ2,subQ1,subQ0,sQuery(id+"F0.wireOp",EDGE,"E37"),sQuery(id+"F0.wireOp",EDGE,"E38")])],"isStart":true}),makeQuery(id+"F6.opExtrude","CAP_FACE",FACE,{"disambiguationData":[OSD([subQ11,subQ10,subQ9,subQ8])],"isStart":true}),makeQuery(id+"F6.opExtrude","CAP_FACE",FACE,{"disambiguationData":[OSD([subQ7,subQ6,subQ5,subQ4])],"isStart":true})]}),makeQuery(id+"F9.opExtrude","CAP_FACE",FACE,{"disambiguationData":[OSD([subQ3])],"isStart":true}),makeQuery(id+"F9.opExtrude","CAP_FACE",FACE,{"disambiguationData":[OSD([subQ2])],"isStart":true}),makeQuery(id+"F9.opExtrude","CAP_FACE",FACE,{"disambiguationData":[OSD([subQ1])],"isStart":true}),makeQuery(id+"F9.opExtrude","CAP_FACE",FACE,{"disambiguationData":[OSD([subQ0])],"isStart":true})]}),makeQuery(id+"F10.opExtrude","SWEPT_FACE",FACE,{"disambiguationData":[OSD([sQuery(id+"F2.wireOp",EDGE,"E72")])]})]});}
            fillet(context, id + "F11", {"entities" : qUnion([Q0, Q1, Q2, Q3]), "radius" : 1 * mm, "tangentPropagation" : true, "allowEdgeOverflow" : false});
        }
        {
            var Q0;
            {var subQ0=sQuery(id+"F0.wireOp",EDGE,"E33");var subQ1=sQuery(id+"F0.wireOp",EDGE,"E32");var subQ2=sQuery(id+"F0.wireOp",EDGE,"E28");var subQ3=sQuery(id+"F0.wireOp",EDGE,"E27");var subQ4=sQuery(id+"F0.wireOp",EDGE,"E24");var subQ5=sQuery(id+"F0.wireOp",EDGE,"E23");var subQ6=sQuery(id+"F0.wireOp",EDGE,"E20");var subQ7=sQuery(id+"F0.wireOp",EDGE,"E19");var subQ8=sQuery(id+"F0.wireOp",EDGE,"E22");var subQ9=sQuery(id+"F0.wireOp",EDGE,"E21");var subQ10=sQuery(id+"F0.wireOp",EDGE,"E13");var subQ11=sQuery(id+"F0.wireOp",EDGE,"E12");Q0=makeQuery(id+"F9.boolean.opBoolean","MERGE",FACE,{"derivedFrom":[makeQuery(id+"F6.boolean.opBoolean","MERGE",FACE,{"derivedFrom":[makeQuery(id+"F1.opExtrude","CAP_FACE",FACE,{"disambiguationData":[OSD([sQuery(id+"F0.wireOp",EDGE,"E0"),sQuery(id+"F0.wireOp",EDGE,"E1"),sQuery(id+"F0.wireOp",EDGE,"E8"),sQuery(id+"F0.wireOp",EDGE,"E9"),sQuery(id+"F0.wireOp",EDGE,"E10"),sQuery(id+"F0.wireOp",EDGE,"E11"),subQ11,subQ10,sQuery(id+"F0.wireOp",EDGE,"E15"),sQuery(id+"F0.wireOp",EDGE,"E16"),subQ7,subQ6,subQ9,subQ8,subQ5,subQ4,subQ3,subQ2,subQ1,subQ0,sQuery(id+"F0.wireOp",EDGE,"E37"),sQuery(id+"F0.wireOp",EDGE,"E38")])],"isStart":false}),makeQuery(id+"F6.opExtrude","CAP_FACE",FACE,{"disambiguationData":[OSD([subQ11,subQ10,subQ9,subQ8])],"isStart":false}),makeQuery(id+"F6.opExtrude","CAP_FACE",FACE,{"disambiguationData":[OSD([subQ7,subQ6,subQ5,subQ4])],"isStart":false})]}),makeQuery(id+"F9.opExtrude","CAP_FACE",FACE,{"disambiguationData":[OSD([subQ3])],"isStart":false}),makeQuery(id+"F9.opExtrude","CAP_FACE",FACE,{"disambiguationData":[OSD([subQ2])],"isStart":false}),makeQuery(id+"F9.opExtrude","CAP_FACE",FACE,{"disambiguationData":[OSD([subQ1])],"isStart":false}),makeQuery(id+"F9.opExtrude","CAP_FACE",FACE,{"disambiguationData":[OSD([subQ0])],"isStart":false})]});}
            var sketch = newSketch(context, id + "F12", { "sketchPlane" : qUnion([Q0])});
            skCircle(sketch, "E75", {"center": v(128.1, 78.07) * mm, "radius": 1.5 * mm});
            skCircle(sketch, "E76", {"center": v(114.87, 69.32) * mm, "radius": 1.5 * mm});
            skCircle(sketch, "E77", {"center": v(130.21, 32.35) * mm, "radius": 1.5 * mm});
            skCircle(sketch, "E78", {"center": v(145.71, 35.4) * mm, "radius": 1.5 * mm});
            skSolve(sketch);
        }
        {
            var Q0;
            Q0=qSketchRegion(id+"F12",true);
            extrude(context, id + "F13", {"entities" : qUnion([Q0]), "operationType" : NewBodyOperationType.REMOVE, "oppositeDirection" : true, "depth" : 25 * mm});
        }
        {
            var Q0;
            {var subQ1=makeQuery(id+"F1.opExtrude","CAP_EDGE",EDGE,{"disambiguationData":[OSD([sQuery(id+"F0.wireOp",EDGE,"E20")])],"isStart":false});Q0=makeQuery(id+"F2.imprint","IMPRINT",FACE,{"disambiguationData":[TD([[makeQuery(id+"F2.imprint","IMPRINT",EDGE,{"derivedFrom":subQ1}),1.0]])]});}
            var sketch = newSketch(context, id + "F14", { "sketchPlane" : qUnion([Q0])});
            skCircle(sketch, "E79", {"center": v(107.2, 92.04) * mm, "radius": 2 * mm});
            skCircle(sketch, "E80", {"center": v(107.2, 92.04) * mm, "radius": 1.5 * mm});
            skSolve(sketch);
        }
        {
            var Q0;
            Q0=qSketchRegion(id+"F14",true);
            extrude(context, id + "F15", {"entities" : qUnion([Q0]), "operationType" : NewBodyOperationType.ADD, "oppositeDirection" : true, "depth" : 2.5 * mm});
        }
    });
